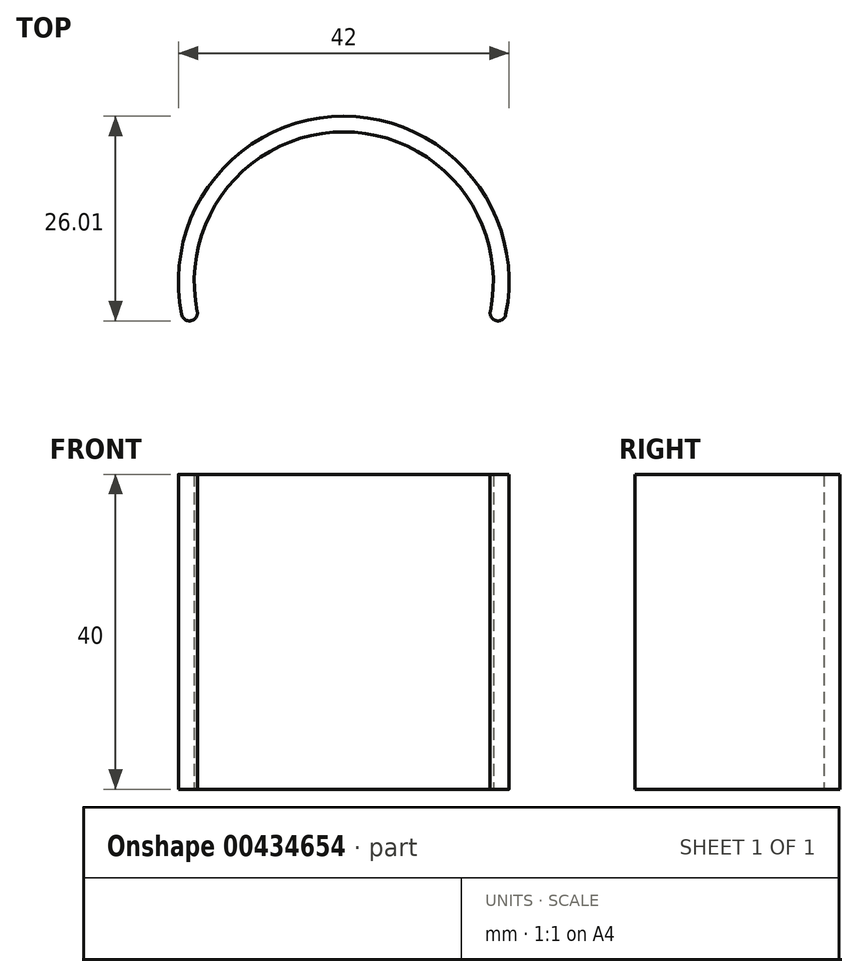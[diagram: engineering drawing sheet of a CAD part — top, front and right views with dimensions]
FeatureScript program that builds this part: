
annotation { "Feature Type Name" : "Feature", "Feature Type Description" : "" }
export const myFeature = defineFeature(function(context is Context, id is Id, definition is map)
    precondition{}
    {
        {
            var Q0;
            Q0=qCreatedBy(makeId("Top.planeOp"),FACE);
            var sketch = newSketch(context, id + "F0", { "sketchPlane" : qUnion([Q0])});
            skArc(sketch, "E0", {"start": v(18.61, -3.8) * mm, "mid": v(0, 19) * mm, "end": v(-18.61, -3.8) * mm});
            skArc(sketch, "E1.0", {"start": v(20.57, -4.2) * mm, "mid": v(0, 21) * mm, "end": v(-20.57, -4.2) * mm});
            skArc(sketch, "E2", {"start": v(-20.57, -4.2) * mm, "mid": v(-19.4, -4.99) * mm, "end": v(-18.61, -3.8) * mm});
            skArc(sketch, "E3", {"start": v(18.61, -3.8) * mm, "mid": v(19.4, -4.99) * mm, "end": v(20.57, -4.2) * mm});
            skSolve(sketch);
        }
        {
            var Q0;
            Q0=makeQuery(id+"F0.imprint","IMPRINT",FACE,{"disambiguationData":[TD([[makeQuery(id+"F0.imprint","IMPRINT",EDGE,{"derivedFrom":sQuery(id+"F0.wireOp",EDGE,"E0")}),-1.0]])]});
            extrude(context, id + "F1", {"entities" : qUnion([Q0]), "depth" : 40 * mm});
        }
    });
